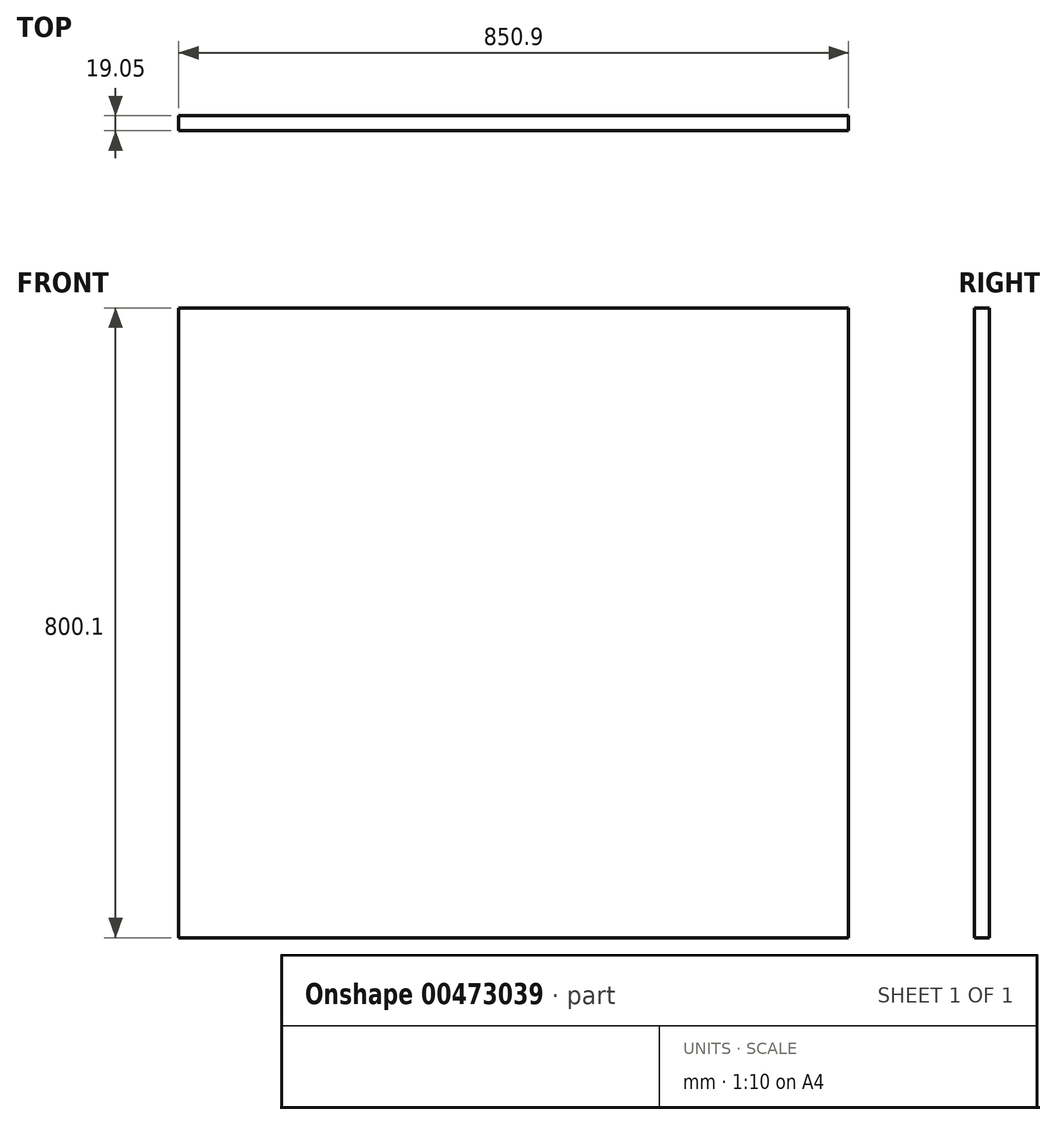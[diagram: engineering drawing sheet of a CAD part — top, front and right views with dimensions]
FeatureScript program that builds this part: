
annotation { "Feature Type Name" : "Feature", "Feature Type Description" : "" }
export const myFeature = defineFeature(function(context is Context, id is Id, definition is map)
    precondition{}
    {
        {
            var Q0;
            Q0=qCreatedBy(makeId("Front.planeOp"),FACE);
            var sketch = newSketch(context, id + "F0", { "sketchPlane" : qUnion([Q0])});
            skLineSegment(sketch, "E0.bottom", {"start": v(425.45, 400.05) * mm, "end": v(-425.45, 400.05) * mm});
            skLineSegment(sketch, "E0.top", {"start": v(425.45, -400.05) * mm, "end": v(-425.45, -400.05) * mm});
            skLineSegment(sketch, "E0.left", {"start": v(425.45, 400.05) * mm, "end": v(425.45, -400.05) * mm});
            skLineSegment(sketch, "E0.right", {"start": v(-425.45, 400.05) * mm, "end": v(-425.45, -400.05) * mm});
            skPoint(sketch, "E0.middle", {"position": v(0, 0) * mm});
            skSolve(sketch);
        }
        {
            var Q0;
            Q0=makeQuery(id+"F0.imprint","IMPRINT",FACE,{"disambiguationData":[TD([[makeQuery(id+"F0.imprint","IMPRINT",EDGE,{"derivedFrom":sQuery(id+"F0.wireOp",EDGE,"E0.bottom")}),1.0]])]});
            extrude(context, id + "F1", {"entities" : qUnion([Q0]), "depth" : 19.05 * mm});
        }
    });
